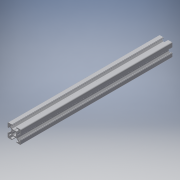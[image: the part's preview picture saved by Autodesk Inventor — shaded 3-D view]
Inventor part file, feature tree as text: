
AUTODESK INVENTOR PART (.ipt)
format: ipt  version: 2016 (Build 200138000, 138)  size: 310,784 bytes
history: native  units: in
note: dims shown in document units (in); Inventor stores cm internally (conversion verified against a paired STEP export)
features: other x3, extrude x1, sketch x1
ambient origin geometry x8: Origin, YZ Plane, XZ Plane, XY Plane, X Axis, Y Axis, Z Axis, Center Point
bodies: Solid1 (feature_tree)
feature tree (5):
  other  "Blocks"
  extrude  "Extrusion1"  [1 undecoded]
  sketch  "Sketch1"  dims[d1=0.0in]
  other  "20x20"
  other  "20x20:1"
note: 1 required parameter value undecoded (feature->parameter linkage not recoverable at this tier; creation-order binding heuristic only, values carry confidence <= 0.55)
